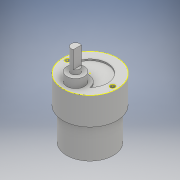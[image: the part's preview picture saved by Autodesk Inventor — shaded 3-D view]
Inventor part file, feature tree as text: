
AUTODESK INVENTOR PART (.ipt)
format: ipt  version: 2018 (Build 220112000, 112)  size: 154,112 bytes
history: native  units: mm
features: extrude x7, sketch x7, projected_geometry x1
ambient origin geometry x8: Origin, YZ Plane, XZ Plane, XY Plane, X Axis, Y Axis, Z Axis, Center Point
bodies: Solid1 (feature_tree)
feature tree (15):
  extrude  "Extrusion1"  Depth=31.0mm
  sketch  "Sketch2"  dims[d2=3.4mm d3=3.4mm]
  extrude  "Extrusion2"  Depth=3.4mm
  extrude  "Extrusion3"  Depth=4.5mm
  extrude  "Extrusion4"  Depth=12.0mm
  extrude  "Extrusion5"  Depth=1.0mm TaperAngle=0.0deg
  extrude  "Extrusion6"  Depth=15.0mm TaperAngle=0.0deg
  extrude  "Extrusion7"  Depth=12.0mm TaperAngle=0.0deg
  sketch  "Sketch7"  dims[d19=14.5mm d20=0.0mm d21=12.0mm d22=0.0mm d23=32.0mm d24=22.0mm d25=0.0mm]
  sketch  "Sketch1"  dims[d0=37.0mm d1=31.0mm]
  sketch  "Sketch3"  dims[d4=4.5mm d5=0.0mm d6=24.0mm]
  projected_geometry  "Projected Loop1"
  sketch  "Sketch4"  dims[d10=17.2mm d11=12.0mm]
  sketch  "Sketch5"  dims[d12=6.0mm d13=0.0mm d14=1.0mm d15=0.0mm]
  sketch  "Sketch6"  dims[d16=6.0mm d17=15.0mm d18=0.0mm]
